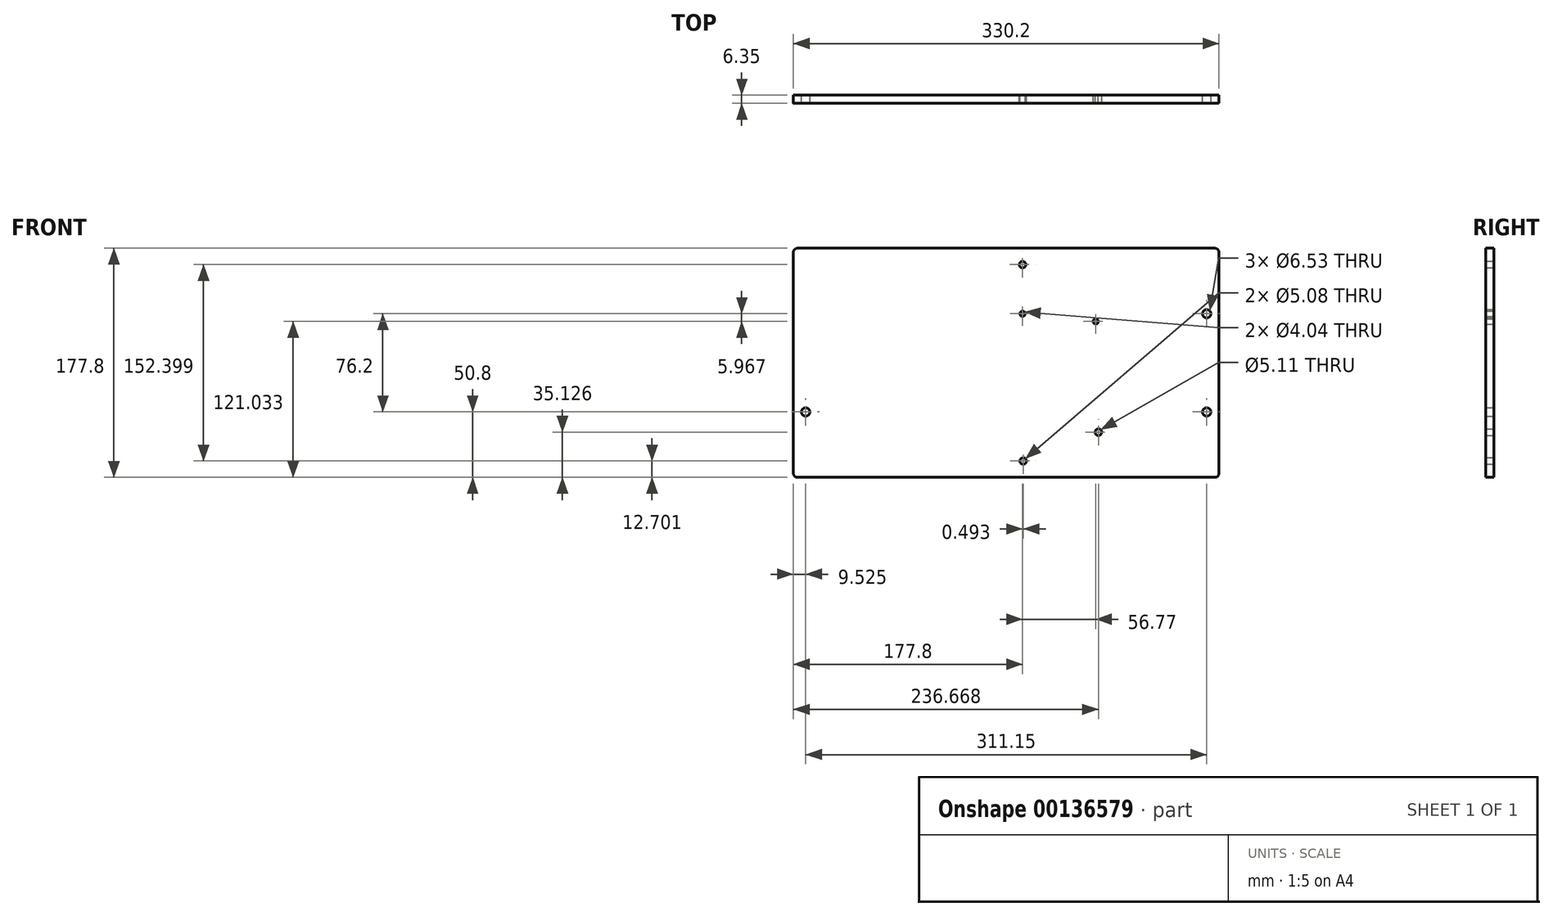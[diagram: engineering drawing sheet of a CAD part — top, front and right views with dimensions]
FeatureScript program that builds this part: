
annotation { "Feature Type Name" : "Feature", "Feature Type Description" : "" }
export const myFeature = defineFeature(function(context is Context, id is Id, definition is map)
    precondition{}
    {
        {
            var Q0;
            Q0=qCreatedBy(makeId("Front.planeOp"),FACE);
            var sketch = newSketch(context, id + "F0", { "sketchPlane" : qUnion([Q0])});
            skLineSegment(sketch, "E0.bottom", {"start": v(3.18, 0) * mm, "end": v(327.03, 0) * mm});
            skLineSegment(sketch, "E0.top", {"start": v(3.17, 177.8) * mm, "end": v(327.03, 177.8) * mm});
            skLineSegment(sketch, "E0.left", {"start": v(0, 3.17) * mm, "end": v(0, 174.62) * mm});
            skLineSegment(sketch, "E0.right", {"start": v(330.2, 3.17) * mm, "end": v(330.2, 174.62) * mm});
            skPoint(sketch, "E1", {"position": v(177.8, 165.1) * mm});
            skPoint(sketch, "E2", {"position": v(178.3, 12.7) * mm});
            skLineSegment(sketch, "E3", {"start": v(0, 127) * mm, "end": v(330.2, 127) * mm, "construction": true});
            skLineSegment(sketch, "E4", {"start": v(0, 50.8) * mm, "end": v(330.2, 50.8) * mm, "construction": true});
            skLineSegment(sketch, "E5", {"start": v(0, 88.9) * mm, "end": v(330.2, 88.9) * mm, "construction": true});
            skLineSegment(sketch, "E6", {"start": v(320.68, 177.8) * mm, "end": v(320.68, 0) * mm, "construction": true});
            skPoint(sketch, "E7", {"position": v(320.68, 127) * mm});
            skPoint(sketch, "E8", {"position": v(320.68, 50.8) * mm});
            skPoint(sketch, "E9.visualSharp", {"position": v(0, 177.8) * mm});
            skArc(sketch, "E9.filletArc", {"start": v(3.17, 177.8) * mm, "mid": v(0.93, 176.87) * mm, "end": v(0, 174.62) * mm});
            skPoint(sketch, "E10.visualSharp", {"position": v(0, 0) * mm});
            skArc(sketch, "E10.filletArc", {"start": v(0, 3.17) * mm, "mid": v(0.93, 0.93) * mm, "end": v(3.18, 0) * mm});
            skPoint(sketch, "E11.visualSharp", {"position": v(330.2, 0) * mm});
            skArc(sketch, "E11.filletArc", {"start": v(327.03, 0) * mm, "mid": v(329.27, 0.93) * mm, "end": v(330.2, 3.18) * mm});
            skPoint(sketch, "E12.visualSharp", {"position": v(330.2, 177.8) * mm});
            skArc(sketch, "E12.filletArc", {"start": v(330.2, 174.62) * mm, "mid": v(329.27, 176.87) * mm, "end": v(327.03, 177.8) * mm});
            skCircle(sketch, "E13", {"center": v(178.3, 12.7) * mm, "radius": 2.54 * mm});
            skCircle(sketch, "E14", {"center": v(177.8, 165.1) * mm, "radius": 2.54 * mm});
            skCircle(sketch, "E15", {"center": v(9.53, 50.8) * mm, "radius": 3.26 * mm});
            skCircle(sketch, "E16", {"center": v(320.68, 127) * mm, "radius": 3.26 * mm});
            skCircle(sketch, "E17", {"center": v(320.68, 50.8) * mm, "radius": 3.26 * mm});
            skLineSegment(sketch, "E18", {"start": v(330.2, 31.75) * mm, "end": v(0, 31.75) * mm, "construction": true});
            skLineSegment(sketch, "E19", {"start": v(177.8, 165.1) * mm, "end": v(177.8, -146.05) * mm, "construction": true});
            skCircle(sketch, "E20", {"center": v(177.8, -146.05) * mm, "radius": 273.05 * mm, "construction": true});
            skCircle(sketch, "E21", {"center": v(177.8, -146.05) * mm, "radius": 190.5 * mm, "construction": true});
            skLineSegment(sketch, "E22", {"start": v(177.8, -146.05) * mm, "end": v(206.34, 125.5) * mm, "construction": true});
            skLineSegment(sketch, "E23", {"start": v(177.8, -146.05) * mm, "end": v(236.67, 35.13) * mm, "construction": true});
            skLineSegment(sketch, "E24", {"start": v(177.8, -146.05) * mm, "end": v(234.57, 121.03) * mm, "construction": true});
            skLineSegment(sketch, "E25", {"start": v(177.8, -146.05) * mm, "end": v(177.8, 127) * mm, "construction": true});
            skCircle(sketch, "E26", {"center": v(234.57, 121.03) * mm, "radius": 2.02 * mm});
            skCircle(sketch, "E27", {"center": v(177.8, 127) * mm, "radius": 2.02 * mm});
            skCircle(sketch, "E28", {"center": v(236.67, 35.13) * mm, "radius": 2.55 * mm});
            skSolve(sketch);
        }
        {
            var Q0;
            Q0=makeQuery(id+"F0.imprint","IMPRINT",FACE,{"disambiguationData":[TD([[makeQuery(id+"F0.imprint","IMPRINT",EDGE,{"derivedFrom":sQuery(id+"F0.wireOp",EDGE,"E0.bottom")}),1.0]])]});
            extrude(context, id + "F1", {"entities" : qUnion([Q0]), "depth" : 6.35 * mm});
        }
    });
